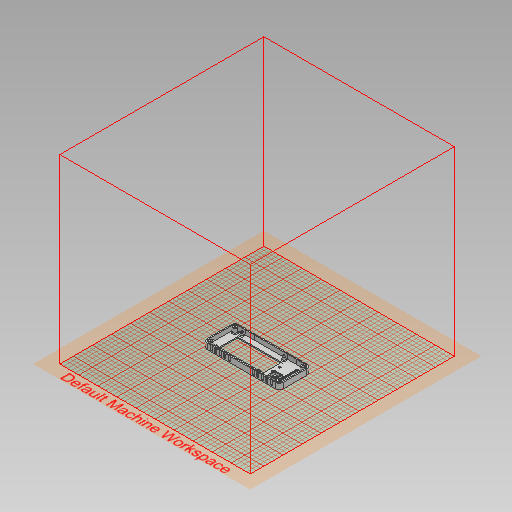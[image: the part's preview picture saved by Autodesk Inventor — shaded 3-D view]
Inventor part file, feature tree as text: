
AUTODESK INVENTOR PART (.ipt)
format: ipt  version: 2019 (Build 230136000, 136)  size: 1,781,760 bytes
history: native  units: mm
features: sketch x12, projected_geometry x11, extrude x10, chamfer x3, fillet x2, plane x2, mirror x2, other x1, pattern_linear x1, hole x1
ambient origin geometry x8: Origin, YZ Plane, XZ Plane, XY Plane, X Axis, Y Axis, Z Axis, Center Point
bodies: Body1 (feature_tree)
feature tree (45):
  other  "Sólido1"
  extrude  "Extrusión1"  Depth=40.5mm
  extrude  "Extrusión2"  Depth=20.0mm
  extrude  "Extrusión3"  Depth=2.5mm TaperAngle=0.0deg
  extrude  "Extrusión4"  Depth=6.0mm
  fillet  "Empalme1"  Radius=6.0mm
  extrude  "Extrusión5"  Depth=6.0mm
  extrude  "Extrusión7"  Depth=6.0mm TaperAngle=0.0deg
  pattern_linear  "Patrón rectangular1"  Spacing1=19.0mm  [1 undecoded]
  plane  "Plano de trabajo1"
  mirror  "Simetría1"
  mirror  "Simetría2"
  sketch  "Boceto12"  dims[d20=3.0mm]
  hole  "Agujero2"  [1 undecoded]
  extrude  "Extrusión8"  Depth=15.0mm
  chamfer  "Chaflán2"  Distance=10.0mm
  extrude  "Extrusión10"  Depth=15.0mm
  chamfer  "Chaflán3"  Distance=5.3mm
  extrude  "Extrusión11"  Depth=2.0mm
  fillet  "Empalme2"  Radius=2.5mm
  extrude  "Extrusión12"  Depth=2.0mm
  chamfer  "Chaflán4"  Distance=2.5mm
  sketch  "Boceto1"  dims[d5=97.6mm d6=40.5mm]
  sketch  "Boceto2"  dims[d7=70.0mm d8=20.0mm]
  projected_geometry  "Contorno proyectado1"
  sketch  "Boceto3"  dims[d9=50.0mm d10=2.5mm d11=0.0mm]
  projected_geometry  "Contorno proyectado2"
  projected_geometry  "Contorno proyectado3"
  projected_geometry  "Contorno proyectado4"
  projected_geometry  "Contorno proyectado5"
  sketch  "Boceto4"  dims[d12=93.0mm d13=55.0mm d14=6.0mm]
  projected_geometry  "Contorno proyectado6"
  sketch  "Boceto6"  dims[d15=6.0mm d16=6.0mm]
  projected_geometry  "Contorno proyectado7"
  sketch  "Boceto10"  dims[d17=6.0mm d18=6.0mm d19=0.0mm]
  plane  "Plano de trabajo2"
  sketch  "Boceto13"  dims[d21=3.0mm]
  projected_geometry  "Contorno proyectado9"
  sketch  "Boceto14"  dims[d22=3.0mm]
  projected_geometry  "Contorno proyectado10"
  sketch  "Boceto16"  dims[d23=3.0mm]
  sketch  "Boceto18"  dims[d24=2.5mm d25=0.0mm]
  projected_geometry  "Contorno proyectado12"
  sketch  "Boceto19"  dims[d26=22.0mm d27=19.0mm d28=7.3mm d29=15.0mm d30=10.0mm d31=15.0mm d32=5.3mm d33=5.3mm d34=2.5mm d35=0.0mm d36=9.0mm d37=2.5mm d38=25.0mm d39=0.0mm d53=5.0mm d54=15.0mm d55=1.2mm d56=0.0mm d57=50.0mm d59=10.0mm d60=15.0mm d64=4.5mm d65=6.0mm d66=4.0mm d67=2.0mm d68=90.0deg d69=20.0mm d70=20.594885mm d71=2.0mm d72=2.0mm d73=2.0mm d74=2.0mm d75=10.0mm d76=0.0mm d80=9.0mm d85=2.0mm d86=2.0mm d87=45.0deg d88=1.5mm d89=0.0mm d90=1.5mm d91=2.0mm d92=45.0deg d93=2.0mm d94=1.5mm d95=0.5mm d96=0.0mm d97=2.0mm d98=12.3mm d99=12.3mm d100=2.0mm d101=5.0mm d102=0.0mm d103=1.0mm d104=2.0mm d105=45.0deg]
  projected_geometry  "Contorno proyectado13"
note: 2 required parameter values undecoded (feature->parameter linkage not recoverable at this tier; creation-order binding heuristic only, values carry confidence <= 0.55)
